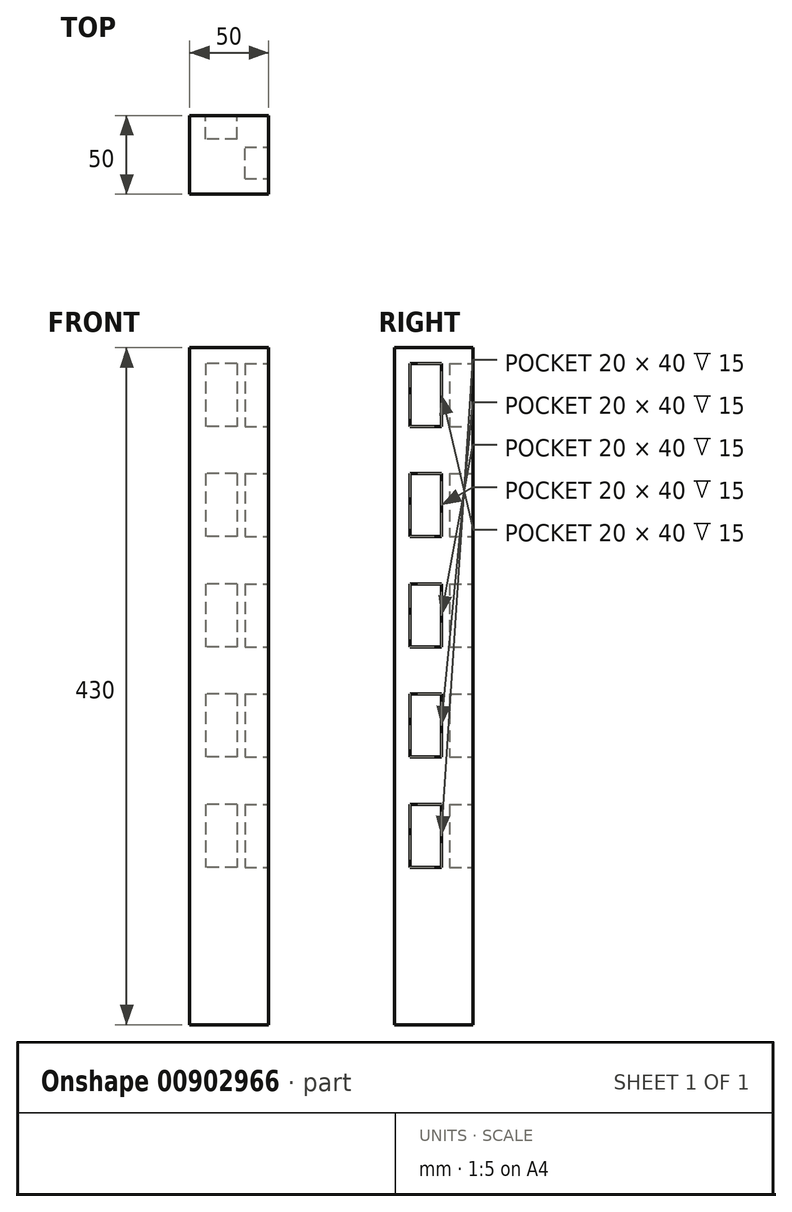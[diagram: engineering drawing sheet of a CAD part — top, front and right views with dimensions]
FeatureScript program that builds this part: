
annotation { "Feature Type Name" : "Feature", "Feature Type Description" : "" }
export const myFeature = defineFeature(function(context is Context, id is Id, definition is map)
    precondition{}
    {
        {
            var Q0;
            Q0=qCreatedBy(makeId("Top.planeOp"),FACE);
            var sketch = newSketch(context, id + "F0", { "sketchPlane" : qUnion([Q0])});
            skLineSegment(sketch, "E0.bottom", {"start": v(0, 0) * mm, "end": v(50, 0) * mm});
            skLineSegment(sketch, "E0.top", {"start": v(0, -50) * mm, "end": v(50, -50) * mm});
            skLineSegment(sketch, "E0.left", {"start": v(0, 0) * mm, "end": v(0, -50) * mm});
            skLineSegment(sketch, "E0.right", {"start": v(50, 0) * mm, "end": v(50, -50) * mm});
            skSolve(sketch);
        }
        {
            var Q0;
            Q0 = qSketchRegion(id + "F0", true);
            extrude(context, id + "F1", {"entities" : qUnion([Q0]), "depth" : 430 * mm, "offsetDistance" : 25 * mm});
        }
        {
            var Q0;
            Q0=makeQuery(id+"F1.opExtrude","SWEPT_FACE",FACE,{"disambiguationData":[OSD([sQuery(id+"F0.wireOp",EDGE,"E0.right")])]});
            var sketch = newSketch(context, id + "F2", { "sketchPlane" : qUnion([Q0])});
            skLineSegment(sketch, "E1.bottom", {"start": v(-40, 420) * mm, "end": v(-20, 420) * mm});
            skLineSegment(sketch, "E1.top", {"start": v(-40, 380) * mm, "end": v(-20, 380) * mm});
            skLineSegment(sketch, "E1.left", {"start": v(-40, 420) * mm, "end": v(-40, 380) * mm});
            skLineSegment(sketch, "E1.right", {"start": v(-20, 420) * mm, "end": v(-20, 380) * mm});
            skLineSegment(sketch, "E2.bottom", {"start": v(-40, 350) * mm, "end": v(-20, 350) * mm});
            skLineSegment(sketch, "E2.top", {"start": v(-40, 310) * mm, "end": v(-20, 310) * mm});
            skLineSegment(sketch, "E2.left", {"start": v(-40, 350) * mm, "end": v(-40, 310) * mm});
            skLineSegment(sketch, "E2.right", {"start": v(-20, 350) * mm, "end": v(-20, 310) * mm});
            skLineSegment(sketch, "E3.bottom", {"start": v(-40, 280) * mm, "end": v(-20, 280) * mm});
            skLineSegment(sketch, "E3.top", {"start": v(-40, 240) * mm, "end": v(-20, 240) * mm});
            skLineSegment(sketch, "E3.left", {"start": v(-40, 280) * mm, "end": v(-40, 240) * mm});
            skLineSegment(sketch, "E3.right", {"start": v(-20, 280) * mm, "end": v(-20, 240) * mm});
            skLineSegment(sketch, "E4.bottom", {"start": v(-40, 210) * mm, "end": v(-20, 210) * mm});
            skLineSegment(sketch, "E4.top", {"start": v(-40, 170) * mm, "end": v(-20, 170) * mm});
            skLineSegment(sketch, "E4.left", {"start": v(-40, 210) * mm, "end": v(-40, 170) * mm});
            skLineSegment(sketch, "E4.right", {"start": v(-20, 210) * mm, "end": v(-20, 170) * mm});
            skLineSegment(sketch, "E5.bottom", {"start": v(-40, 140) * mm, "end": v(-20, 140) * mm});
            skLineSegment(sketch, "E5.top", {"start": v(-40, 100) * mm, "end": v(-20, 100) * mm});
            skLineSegment(sketch, "E5.left", {"start": v(-40, 140) * mm, "end": v(-40, 100) * mm});
            skLineSegment(sketch, "E5.right", {"start": v(-20, 140) * mm, "end": v(-20, 100) * mm});
            skSolve(sketch);
        }
        {
            var Q0;
            Q0 = qSketchRegion(id + "F2", true);
            extrude(context, id + "F3", {"entities" : qUnion([Q0]), "operationType" : NewBodyOperationType.REMOVE, "oppositeDirection" : true, "depth" : 15 * mm, "offsetDistance" : 25 * mm});
        }
        {
            var Q0;
            Q0=makeQuery(id+"F1.opExtrude","SWEPT_FACE",FACE,{"disambiguationData":[OSD([sQuery(id+"F0.wireOp",EDGE,"E0.bottom")])]});
            var sketch = newSketch(context, id + "F4", { "sketchPlane" : qUnion([Q0])});
            skLineSegment(sketch, "E6.bottom", {"start": v(-30, 420) * mm, "end": v(-10, 420) * mm});
            skLineSegment(sketch, "E6.top", {"start": v(-30, 380) * mm, "end": v(-10, 380) * mm});
            skLineSegment(sketch, "E6.left", {"start": v(-30, 420) * mm, "end": v(-30, 380) * mm});
            skLineSegment(sketch, "E6.right", {"start": v(-10, 420) * mm, "end": v(-10, 380) * mm});
            skLineSegment(sketch, "E7.bottom", {"start": v(-30, 350) * mm, "end": v(-10, 350) * mm});
            skLineSegment(sketch, "E7.top", {"start": v(-30, 310) * mm, "end": v(-10, 310) * mm});
            skLineSegment(sketch, "E7.left", {"start": v(-30, 350) * mm, "end": v(-30, 310) * mm});
            skLineSegment(sketch, "E7.right", {"start": v(-10, 350) * mm, "end": v(-10, 310) * mm});
            skLineSegment(sketch, "E8.bottom", {"start": v(-30, 280) * mm, "end": v(-10, 280) * mm});
            skLineSegment(sketch, "E8.top", {"start": v(-30, 240) * mm, "end": v(-10, 240) * mm});
            skLineSegment(sketch, "E8.left", {"start": v(-30, 280) * mm, "end": v(-30, 240) * mm});
            skLineSegment(sketch, "E8.right", {"start": v(-10, 280) * mm, "end": v(-10, 240) * mm});
            skLineSegment(sketch, "E9.bottom", {"start": v(-30, 210) * mm, "end": v(-10, 210) * mm});
            skLineSegment(sketch, "E9.top", {"start": v(-30, 170) * mm, "end": v(-10, 170) * mm});
            skLineSegment(sketch, "E9.left", {"start": v(-30, 210) * mm, "end": v(-30, 170) * mm});
            skLineSegment(sketch, "E9.right", {"start": v(-10, 210) * mm, "end": v(-10, 170) * mm});
            skLineSegment(sketch, "E10.bottom", {"start": v(-30, 140) * mm, "end": v(-10, 140) * mm});
            skLineSegment(sketch, "E10.top", {"start": v(-30, 100) * mm, "end": v(-10, 100) * mm});
            skLineSegment(sketch, "E10.left", {"start": v(-30, 140) * mm, "end": v(-30, 100) * mm});
            skLineSegment(sketch, "E10.right", {"start": v(-10, 140) * mm, "end": v(-10, 100) * mm});
            skSolve(sketch);
        }
        {
            var Q0;
            Q0 = qSketchRegion(id + "F4", true);
            extrude(context, id + "F5", {"entities" : qUnion([Q0]), "operationType" : NewBodyOperationType.REMOVE, "oppositeDirection" : true, "depth" : 15 * mm, "offsetDistance" : 25 * mm});
        }
    });
